# Revit family: Faucet_Lavatory-DXV-Fitzgerald-D35160102_Series
name_source: partatom
category: Plumbing Fixtures
revit_build: Autodesk Revit 2014 (Build: 20130308_1515(x64)
units: mm (PartAtom-declared; Revit-internal decimal feet)

## types (3) — shared parameters
ADA Compliant = Yes
Assembly Code = D2020300
CW Connection = Yes
CWFU = 1.5
Cold Water Connection Diameter = 3/8"
Default Elevation = 0"
Description = Fitzgerald Monoblock Lavatory Faucet
Flow Rate = 1.2 gpm (4.5 L/min)
HW Connection = Yes
HWFU = 1.5
Height = 8 1/2"
Hot Water Connection Diameter = 0"
Installation Type = Deck Mounted
Length = 5 3/4"
Manufacturer = DXV
Price = Prices may vary. Please consult Manufacturer Representative for most up-to-date price list.
Product Documentation Link = https://dxv01.blob.core.windows.net
Product Page URL = https://www.dxv.com
Revised Date = 10/25/2018
URL = http://www.dxv.com
Vent Connection = No
WFU = 2
Warranty Documentation Link = https://www.dxv.com
Waste Connection = No
Width = 2 5/8"

## per-type parameters (varying)
| type | Finish | Material |
| D35160102.100 | Metal-DXV-100-Polished Chrome | Metal-DXV-100-Polished Chrome |
| D35160102.144 | Metal-DXV-144-Brushed Nickel | Metal-DXV-144-Brushed Nickel |
| D35160102.150 | Metal-DXV-150-Platinum Nickel | Metal-DXV-150-Platinum Nickel |

note: column(s) folded — value = type name in every type: Model

## geometry (parser evidence)
native form markers: Sweep x2
no freeform markers — native parametric forms only
